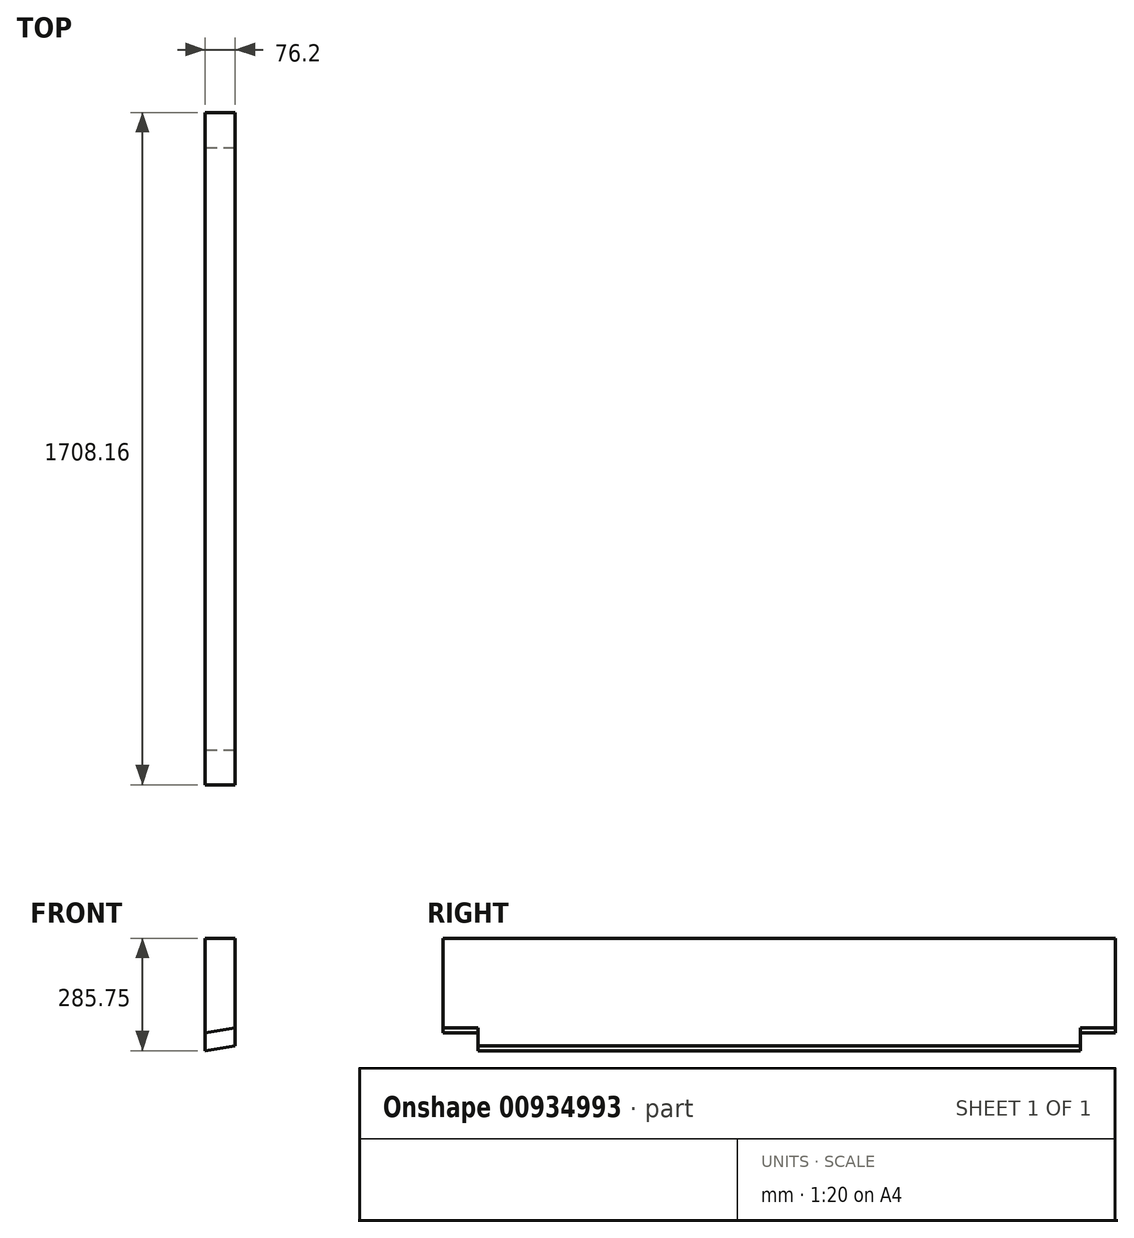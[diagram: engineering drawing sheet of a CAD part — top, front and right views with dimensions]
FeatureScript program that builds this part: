
annotation { "Feature Type Name" : "Feature", "Feature Type Description" : "" }
export const myFeature = defineFeature(function(context is Context, id is Id, definition is map)
    precondition{}
    {
        {
            var Q0;
            Q0=qCreatedBy(makeId("Front.planeOp"),FACE);
            var sketch = newSketch(context, id + "F0", { "sketchPlane" : qUnion([Q0])});
            skLineSegment(sketch, "E0", {"start": v(0, 0) * mm, "end": v(76.2, 0) * mm});
            skLineSegment(sketch, "E1", {"start": v(76.2, 0) * mm, "end": v(76.2, -273.27) * mm});
            skLineSegment(sketch, "E2", {"start": v(76.2, -273.27) * mm, "end": v(0, -285.75) * mm});
            skLineSegment(sketch, "E3", {"start": v(0, -285.75) * mm, "end": v(0, 0) * mm});
            skSolve(sketch);
        }
        {
            var Q0;
            Q0 = qSketchRegion(id + "F0", true);
            extrude(context, id + "F1", {"entities" : qUnion([Q0]), "depth" : 1708.15 * mm, "offsetDistance" : 25.4 * mm, "symmetric" : true});
        }
        {
            var Q0;
            Q0=makeQuery(id+"F1.opExtrude","SWEPT_EDGE",EDGE,{"disambiguationData":[OSD([sQuery(id+"F0.wireOp",EDGE,"E2"),sQuery(id+"F0.wireOp",EDGE,"E3")])]});
            cPlane(context, id + "F2", {"entities" : qUnion([Q0]), "cplaneType" : CPlaneType.LINE_ANGLE, "offset" : 25.4 * mm, "angle" : 80.7 * degree, "width" : 152.4 * mm, "height" : 152.4 * mm});
        }
        {
            var Q0;
            Q0=qCreatedBy(id+"F2.planeOp",FACE);
            var sketch = newSketch(context, id + "F3", { "sketchPlane" : qUnion([Q0])});
            skLineSegment(sketch, "E4.bottom", {"start": v(854.08, -282) * mm, "end": v(765.18, -282) * mm});
            skLineSegment(sketch, "E4.top", {"start": v(854.08, -237.54) * mm, "end": v(765.18, -237.54) * mm});
            skLineSegment(sketch, "E4.left", {"start": v(854.08, -282) * mm, "end": v(854.08, -237.54) * mm});
            skLineSegment(sketch, "E4.right", {"start": v(765.18, -282) * mm, "end": v(765.18, -237.54) * mm});
            skPoint(sketch, "E5.oppositeSnap0", {"position": v(809.63, -237.54) * mm});
            skLineSegment(sketch, "E5.bottom", {"start": v(-765.18, -282) * mm, "end": v(-854.08, -282) * mm});
            skLineSegment(sketch, "E5.top", {"start": v(-765.18, -237.54) * mm, "end": v(-854.08, -237.54) * mm});
            skLineSegment(sketch, "E5.left", {"start": v(-765.18, -282) * mm, "end": v(-765.18, -237.54) * mm});
            skLineSegment(sketch, "E5.right", {"start": v(-854.08, -282) * mm, "end": v(-854.08, -237.54) * mm});
            skSolve(sketch);
        }
        {
            var Q0;
            Q0 = qSketchRegion(id + "F3", true);
            extrude(context, id + "F4", {"entities" : qUnion([Q0]), "operationType" : NewBodyOperationType.REMOVE, "oppositeDirection" : true, "depth" : 254 * mm, "offsetDistance" : 25.4 * mm, "symmetric" : true});
        }
    });
